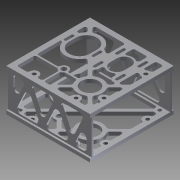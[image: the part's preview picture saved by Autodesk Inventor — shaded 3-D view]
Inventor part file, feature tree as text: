
AUTODESK INVENTOR PART (.ipt)
format: ipt  version: 2012 (Build 160160000, 160)  size: 906,752 bytes
history: native  units: in
note: dims shown in document units (in); Inventor stores cm internally (conversion verified against a paired STEP export)
features: thread x8, extrude x7, sketch x5, fillet x3, projected_geometry x1
ambient origin geometry x8: Origin, YZ Plane, XZ Plane, XY Plane, X Axis, Y Axis, Z Axis, Center Point
bodies: Solid1 (feature_tree)
feature tree (24):
  extrude  "Extrusion1"  Depth=0.1875in
  sketch  "Sketch2"  dims[d4=0.25in d5=0.25in d6=6.0in d7=0.0in]
  extrude  "Extrusion2"  Depth=6.0in TaperAngle=0.0deg
  extrude  "Extrusion3"  Depth=1.25in
  extrude  "Extrusion4"  Depth=0.375in
  fillet  "Fillet2"  Radius=0.875in
  sketch  "Sketch6"  dims[d21=0.125in d22=0.25in d24=0.25in d25=0.125in d27=0.125in d32=0.25in d33=0.0in d35=0.375in d36=0.375in d37=0.375in d38=0.375in d39=0.1719in d40=0.3438in d41=0.3438in d42=0.3438in d43=0.3438in d44=0.125in d46=0.125in d49=0.125in d50=0.125in d51=0.125in d52=0.125in d53=0.125in d54=0.125in d55=0.125in d56=0.125in d57=0.25in d58=0.0in d60=0.3798in d61=0.287in d62=0.287in d63=0.287in d64=0.125in d65=0.125in d66=0.125in d67=0.125in d68=0.125in d69=0.125in d70=0.125in d71=0.125in d72=0.125in d73=0.125in d74=0.375in d76=0.25in d77=0.375in d78=0.375in d79=0.25in d80=0.0in d81=0.25in d88=0.125in d89=1.25in d90=1.75in d91=0.75in d92=0.5in d94=0.2in d96=0.9in d97=1.0in d98=0.5in d99=0.5in d101=2.0in d102=0.2in d103=0.8in d104=0.8in d105=0.7874in d107=1.6in d108=0.7874in d110=1.6in d114=1.0in d115=1.0in d116=1.5in d117=1.0in d119=0.2in d122=4.0in d123=1.3125in d124=0.366in d126=2.0in d127=0.25in d128=0.0in d129=0.375in d131=4.0in d132=0.125in d153=0.25in d154=0.125in d156=0.375in d157=0.375in d160=0.25in d161=0.125in d162=0.25in d163=0.125in d165=0.875in d166=0.125in d168=0.3125in d169=0.125in d170=0.125in d171=1.0in d172=0.25in d177=0.125in d178=0.6in d179=0.25in d180=0.0in d181=0.125in d183=0.25in d185=0.25in d186=0.125in d188=1.5625in d190=1.25in d191=0.366in d193=0.25in d194=0.125in d197=0.875in d198=1.176in d199=0.1in d200=0.0in d201=0.0625in d203=0.25in d207=2.1875in d208=1.75in d211=0.125in d212=0.3in d213=0.5in d214=0.25in d215=0.3125in d220=0.5in d221=1.5in d222=0.25in d224=0.125in d225=2.0in d226=0.35in d227=0.25in d228=1.5in d229=1.5in d230=0.5821in d231=0.25in d232=1.5in d233=0.125in d235=2.25in d236=0.25in d237=1.5in d238=0.3125in d239=0.7874in d241=3.0in d242=0.3937in d244=1.0in d246=1.5in d247=0.7874in d249=3.0in d250=0.3937in d252=1.0in d254=0.5in d255=0.25in d256=0.3125in d257=0.25in d258=0.5in d259=0.3125in d260=0.25in d262=0.625in d264=6.0in d267=0.25in d269=3.0in d270=6.0in d272=0.25in d273=0.125in d274=0.125in d275=0.1435in d276=2.0in d277=1.0in d278=0.0in d279=1.0in d280=0.0in d281=1.0in d282=0.0in d283=1.0in d284=0.0in d285=1.0in d286=0.0in d287=1.0in d288=0.0in d289=1.0in d290=0.0in d291=1.0in d292=0.0in d293=0.125in d294=0.125in d296=0.625in d297=0.25in d298=0.0625in d299=0.125in d300=0.5in d301=1.3125in]
  fillet  "Fillet3"  Radius=0.25in
  extrude  "Extrusion5"  Depth=0.25in
  extrude  "Extrusion6"  Depth=0.25in
  fillet  "Fillet4"  Radius=0.125in
  extrude  "Extrusion7"  Depth=0.125in
  thread  "Thread1"  [1 undecoded]
  thread  "Thread2"  [1 undecoded]
  thread  "Thread3"  [1 undecoded]
  thread  "Thread4"  [1 undecoded]
  thread  "Thread5"  [1 undecoded]
  thread  "Thread6"  [1 undecoded]
  thread  "Thread7"  [1 undecoded]
  thread  "Thread8"  [1 undecoded]
  sketch  "Sketch1"  dims[d1=3.0in d2=0.1875in d3=0.25in]
  sketch  "Sketch4"  dims[d11=1.75in d13=1.25in]
  sketch  "Sketch5"  dims[d15=2.625in d16=1.5in d18=0.375in d19=0.875in d20=0.25in]
  projected_geometry  "Projected Loop1"
note: 8 required parameter values undecoded (feature->parameter linkage not recoverable at this tier; creation-order binding heuristic only, values carry confidence <= 0.55)
